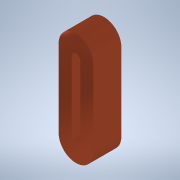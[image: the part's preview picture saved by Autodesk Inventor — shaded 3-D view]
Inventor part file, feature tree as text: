
AUTODESK INVENTOR PART (.ipt)
format: ipt  version: 2022 (Build 260153000, 153)  size: 109,056 bytes
history: native  units: in
note: dims shown in document units (in); Inventor stores cm internally (conversion verified against a paired STEP export)
features: extrude x1, sketch x1
ambient origin geometry x8: Origin, YZ Plane, XZ Plane, XY Plane, X Axis, Y Axis, Z Axis, Center Point
bodies: Solid1 (feature_tree)
feature tree (2):
  extrude  "Extrusion1"  Depth=0.0787in
  sketch  "Sketch1"  dims[d0=0.1969in d1=0.0787in d2=0.0394in d3=0.1181in d4=0.2559in d5=0.0in]
